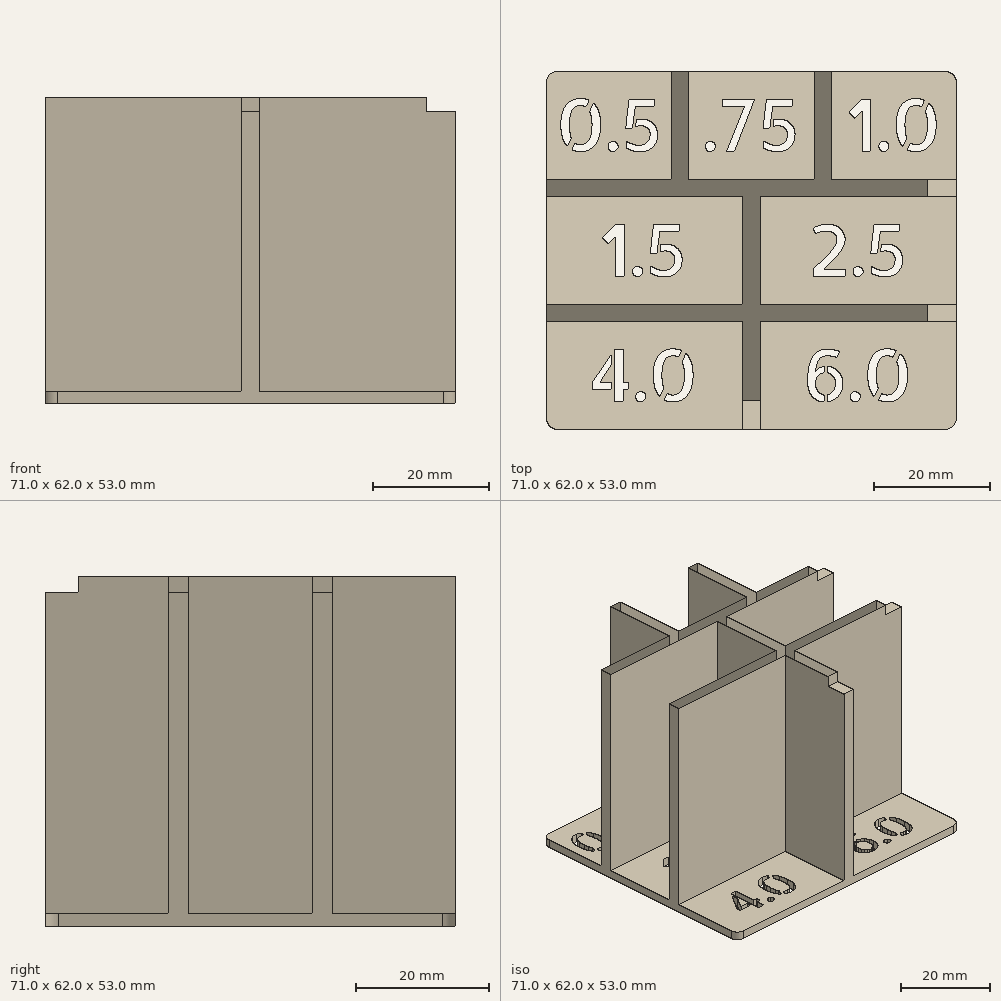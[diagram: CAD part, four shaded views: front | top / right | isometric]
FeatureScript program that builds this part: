
annotation { "Feature Type Name" : "Feature", "Feature Type Description" : "" }
export const myFeature = defineFeature(function(context is Context, id is Id, definition is map)
    precondition{}
    {
        {
            var Q0;
            Q0=qCreatedBy(makeId("Top.planeOp"),FACE);
            var sketch = newSketch(context, id + "F0", { "sketchPlane" : qUnion([Q0])});
            skLineSegment(sketch, "E0.bottom", {"start": v(-35.5, 31) * mm, "end": v(35.5, 31) * mm});
            skLineSegment(sketch, "E0.top", {"start": v(-35.5, -31) * mm, "end": v(35.5, -31) * mm});
            skLineSegment(sketch, "E0.left", {"start": v(-35.5, 31) * mm, "end": v(-35.5, -31) * mm});
            skLineSegment(sketch, "E0.right", {"start": v(35.5, 31) * mm, "end": v(35.5, -31) * mm});
            skSolve(sketch);
        }
        {
            var Q0;
            Q0 = qSketchRegion(id + "F0", true);
            extrude(context, id + "F1", {"entities" : qUnion([Q0]), "depth" : 2 * mm});
        }
        {
            var Q0;
            Q0=makeQuery(id+"F1.opExtrude","CAP_FACE",FACE,{"disambiguationData":[OSD([sQuery(id+"F0.wireOp",EDGE,"E0.bottom"),sQuery(id+"F0.wireOp",EDGE,"E0.top"),sQuery(id+"F0.wireOp",EDGE,"E0.left"),sQuery(id+"F0.wireOp",EDGE,"E0.right")])],"isStart":false});
            var sketch = newSketch(context, id + "F2", { "sketchPlane" : qUnion([Q0])});
            skLineSegment(sketch, "E1", {"start": v(35.5, 12.33) * mm, "end": v(35.5, 9.33) * mm});
            skLineSegment(sketch, "E2", {"start": v(35.5, 9.33) * mm, "end": v(1.5, 9.33) * mm});
            skLineSegment(sketch, "E3", {"start": v(1.5, 9.33) * mm, "end": v(1.5, -9.33) * mm});
            skLineSegment(sketch, "E4", {"start": v(1.5, -9.33) * mm, "end": v(35.5, -9.33) * mm});
            skLineSegment(sketch, "E5", {"start": v(35.5, -9.33) * mm, "end": v(35.5, -12.33) * mm});
            skLineSegment(sketch, "E6", {"start": v(35.5, -12.33) * mm, "end": v(1.5, -12.33) * mm});
            skLineSegment(sketch, "E7", {"start": v(1.5, -12.33) * mm, "end": v(1.5, -31) * mm});
            skLineSegment(sketch, "E8", {"start": v(1.5, -31) * mm, "end": v(-1.5, -31) * mm});
            skLineSegment(sketch, "E9", {"start": v(-1.5, -31) * mm, "end": v(-1.5, -12.33) * mm});
            skLineSegment(sketch, "E10", {"start": v(-1.5, -12.33) * mm, "end": v(-35.5, -12.33) * mm});
            skLineSegment(sketch, "E11", {"start": v(-35.5, -12.33) * mm, "end": v(-35.5, -9.33) * mm});
            skLineSegment(sketch, "E12", {"start": v(-35.5, -9.33) * mm, "end": v(-1.5, -9.33) * mm});
            skLineSegment(sketch, "E13", {"start": v(-1.5, -9.33) * mm, "end": v(-1.5, 9.33) * mm});
            skLineSegment(sketch, "E14", {"start": v(-1.5, 9.33) * mm, "end": v(-35.5, 9.33) * mm});
            skLineSegment(sketch, "E15", {"start": v(-35.5, 9.33) * mm, "end": v(-35.5, 12.33) * mm});
            skLineSegment(sketch, "E16", {"start": v(-35.5, 12.33) * mm, "end": v(-13.83, 12.33) * mm});
            skPoint(sketch, "E17.end.orphan", {"position": v(1.5, 31.5) * mm});
            skPoint(sketch, "E17.start.orphan", {"position": v(-1.5, 31.5) * mm});
            skLineSegment(sketch, "E18", {"start": v(-13.83, 12.33) * mm, "end": v(-13.83, 31) * mm});
            skLineSegment(sketch, "E19", {"start": v(-13.83, 31) * mm, "end": v(-10.83, 31) * mm});
            skLineSegment(sketch, "E20", {"start": v(-10.83, 31) * mm, "end": v(-10.83, 12.3) * mm});
            skLineSegment(sketch, "E21", {"start": v(10.83, 12.3) * mm, "end": v(10.83, 31) * mm});
            skLineSegment(sketch, "E22", {"start": v(10.83, 31) * mm, "end": v(13.83, 31) * mm});
            skLineSegment(sketch, "E23", {"start": v(13.83, 31) * mm, "end": v(13.83, 12.33) * mm});
            skLineSegment(sketch, "E24.trimOffspring", {"start": v(13.83, 12.33) * mm, "end": v(35.5, 12.33) * mm});
            skPoint(sketch, "E25.start.orphan", {"position": v(-1.5, 12.42) * mm});
            skPoint(sketch, "E26.start.orphan", {"position": v(1.5, 12.33) * mm});
            skLineSegment(sketch, "E27", {"start": v(-10.83, 12.3) * mm, "end": v(10.83, 12.3) * mm});
            skSolve(sketch);
        }
        {
            var Q0;
            Q0 = qSketchRegion(id + "F2", true);
            extrude(context, id + "F3", {"entities" : qUnion([Q0]), "operationType" : NewBodyOperationType.ADD, "depth" : 51 * mm});
        }
        {
            var Q0;
            Q0=makeQuery(id+"F1.opExtrude","CAP_FACE",FACE,{"disambiguationData":[OSD([sQuery(id+"F0.wireOp",EDGE,"E0.bottom"),sQuery(id+"F0.wireOp",EDGE,"E0.top"),sQuery(id+"F0.wireOp",EDGE,"E0.left"),sQuery(id+"F0.wireOp",EDGE,"E0.right")])],"isStart":false});
            var sketch = newSketch(context, id + "F4", { "sketchPlane" : qUnion([Q0])});
            skLineSegment(sketch, "E28", {"start": v(-35.5, 0) * mm, "end": v(35.5, 0) * mm, "construction": true});
            skLineSegment(sketch, "E29", {"start": v(-35.5, -21.67) * mm, "end": v(35.5, -21.67) * mm, "construction": true});
            skText(sketch, "E30", { "text": "1.5", "fontName": "AllertaStencil-Regular.ttf"});
            skText(sketch, "E31", { "text": "2.5", "fontName": "AllertaStencil-Regular.ttf"});
            skText(sketch, "E32", { "text": "4.0", "fontName": "AllertaStencil-Regular.ttf"});
            skText(sketch, "E33", { "text": "6.0", "fontName": "AllertaStencil-Regular.ttf"});
            skLineSegment(sketch, "E34", {"start": v(-18.5, -31) * mm, "end": v(-18.5, 9.33) * mm, "construction": true});
            skLineSegment(sketch, "E35", {"start": v(18.5, 9.33) * mm, "end": v(18.5, -31) * mm, "construction": true});
            skLineSegment(sketch, "E36", {"start": v(-24.67, 31) * mm, "end": v(-24.67, 12.33) * mm, "construction": true});
            skLineSegment(sketch, "E37", {"start": v(0, 31) * mm, "end": v(0, 12.3) * mm, "construction": true});
            skLineSegment(sketch, "E38", {"start": v(24.67, 31) * mm, "end": v(24.67, 12.33) * mm, "construction": true});
            skLineSegment(sketch, "E39", {"start": v(-35.5, 21.67) * mm, "end": v(35.5, 21.67) * mm, "construction": true});
            skText(sketch, "E40", { "text": "0.5", "fontName": "AllertaStencil-Regular.ttf"});
            skText(sketch, "E41", { "text": ".75", "fontName": "AllertaStencil-Regular.ttf"});
            skText(sketch, "E42", { "text": "1.0", "fontName": "AllertaStencil-Regular.ttf"});
            const initialGuessF4  = {"E30": [-0.02613, -0.0045, 1, 0, 0.009], "E31": [0.0097, -0.0045, 1, 0, 0.009], "E32": [-0.02802, -0.02617, 1, 0, 0.009], "E33": [0.00882, -0.02617, 1, 0, 0.009], "E40": [-0.03392, 0.01717, 1, 0, 0.009], "E41": [-0.00838, 0.01717, 1, 0, 0.009], "E42": [0.0165, 0.01717, 1, 0, 0.009]};
            skSetInitialGuess(sketch, initialGuessF4);
            skSolve(sketch);
        }
        {
            var Q0;
            Q0 = qSketchRegion(id + "F4", true);
            var Q1;
            Q1=makeQuery(id+"F1.opExtrude","CAP_FACE",FACE,{"disambiguationData":[OSD([sQuery(id+"F0.wireOp",EDGE,"E0.bottom"),sQuery(id+"F0.wireOp",EDGE,"E0.top"),sQuery(id+"F0.wireOp",EDGE,"E0.left"),sQuery(id+"F0.wireOp",EDGE,"E0.right")])],"isStart":true});
            extrude(context, id + "F5", {"entities" : qUnion([Q0]), "operationType" : NewBodyOperationType.REMOVE, "endBound" : BoundingType.UP_TO_SURFACE, "oppositeDirection" : true, "endBoundEntityFace" : qUnion([Q1]), "depth" : 25 * mm});
        }
        {
            var Q0;
            Q0=makeQuery(id+"F1.opExtrude","SWEPT_EDGE",EDGE,{"disambiguationData":[OSD([sQuery(id+"F0.wireOp",EDGE,"E0.top"),sQuery(id+"F0.wireOp",EDGE,"E0.left")])]});
            var Q1;
            Q1=makeQuery(id+"F1.opExtrude","SWEPT_EDGE",EDGE,{"disambiguationData":[OSD([sQuery(id+"F0.wireOp",EDGE,"E0.bottom"),sQuery(id+"F0.wireOp",EDGE,"E0.left")])]});
            var Q2;
            Q2=makeQuery(id+"F1.opExtrude","SWEPT_EDGE",EDGE,{"disambiguationData":[OSD([sQuery(id+"F0.wireOp",EDGE,"E0.top"),sQuery(id+"F0.wireOp",EDGE,"E0.right")])]});
            var Q3;
            Q3=makeQuery(id+"F1.opExtrude","SWEPT_EDGE",EDGE,{"disambiguationData":[OSD([sQuery(id+"F0.wireOp",EDGE,"E0.bottom"),sQuery(id+"F0.wireOp",EDGE,"E0.right")])]});
            fillet(context, id + "F6", {"entities" : qUnion([Q0, Q1, Q2, Q3]), "radius" : 2 * mm, "tangentPropagation" : true, "allowEdgeOverflow" : false});
        }
        {
            var Q0;
            Q0=makeQuery(id+"F3.opExtrude","CAP_FACE",FACE,{"disambiguationData":[OSD([sQuery(id+"F2.wireOp",EDGE,"E17"),sQuery(id+"F2.wireOp",EDGE,"o9r5JfsR-y7DY-JWNR-HnQB-APG8M1iN6JZY"),sQuery(id+"F2.wireOp",EDGE,"E26"),sQuery(id+"F2.wireOp",EDGE,"E1"),sQuery(id+"F2.wireOp",EDGE,"E2"),sQuery(id+"F2.wireOp",EDGE,"E3"),sQuery(id+"F2.wireOp",EDGE,"E4"),sQuery(id+"F2.wireOp",EDGE,"E5"),sQuery(id+"F2.wireOp",EDGE,"E6"),sQuery(id+"F2.wireOp",EDGE,"E7"),sQuery(id+"F2.wireOp",EDGE,"E8"),sQuery(id+"F2.wireOp",EDGE,"E9"),sQuery(id+"F2.wireOp",EDGE,"E10"),sQuery(id+"F2.wireOp",EDGE,"E11"),sQuery(id+"F2.wireOp",EDGE,"E12"),sQuery(id+"F2.wireOp",EDGE,"E13"),sQuery(id+"F2.wireOp",EDGE,"E14"),sQuery(id+"F2.wireOp",EDGE,"E15"),sQuery(id+"F2.wireOp",EDGE,"E16"),sQuery(id+"F2.wireOp",EDGE,"WffC01qx-3Esz-kBEi-Bbgy-qoGBjE8jmLn6")])],"isStart":false});
            var sketch = newSketch(context, id + "F7", { "sketchPlane" : qUnion([Q0])});
            skLineSegment(sketch, "E43.bottom", {"start": v(35.5, 12.33) * mm, "end": v(30.5, 12.33) * mm});
            skLineSegment(sketch, "E43.top", {"start": v(35.5, 9.33) * mm, "end": v(30.5, 9.33) * mm});
            skLineSegment(sketch, "E43.left", {"start": v(35.5, 12.33) * mm, "end": v(35.5, 9.33) * mm});
            skLineSegment(sketch, "E43.right", {"start": v(30.5, 12.33) * mm, "end": v(30.5, 9.33) * mm});
            skLineSegment(sketch, "E44.bottom", {"start": v(35.5, -9.33) * mm, "end": v(30.5, -9.33) * mm});
            skLineSegment(sketch, "E44.top", {"start": v(35.5, -12.33) * mm, "end": v(30.5, -12.33) * mm});
            skLineSegment(sketch, "E44.left", {"start": v(35.5, -9.33) * mm, "end": v(35.5, -12.33) * mm});
            skLineSegment(sketch, "E44.right", {"start": v(30.5, -9.33) * mm, "end": v(30.5, -12.33) * mm});
            skLineSegment(sketch, "E45.bottom", {"start": v(1.5, -31) * mm, "end": v(-1.5, -31) * mm});
            skLineSegment(sketch, "E45.top", {"start": v(1.5, -26) * mm, "end": v(-1.5, -26) * mm});
            skLineSegment(sketch, "E45.left", {"start": v(1.5, -31) * mm, "end": v(1.5, -26) * mm});
            skLineSegment(sketch, "E45.right", {"start": v(-1.5, -31) * mm, "end": v(-1.5, -26) * mm});
            skSolve(sketch);
        }
        {
            var Q0;
            Q0 = qSketchRegion(id + "F7", true);
            extrude(context, id + "F8", {"entities" : qUnion([Q0]), "operationType" : NewBodyOperationType.REMOVE, "oppositeDirection" : true, "depth" : 2.5 * mm});
        }
    });
